# Revit family: Faucet_Touchless-Lavatory-KOHLER-Kumin-K-106K37
name_source: partatom
category: Plumbing Fixtures
units: mm (PartAtom-declared; Revit-internal decimal feet)

## family parameters
Cut with Voids When Loaded = No
Host = Face
OmniClass Number = 23.31.11.00
OmniClass Title = Faucets
Part Type = Normal
Room Calculation Point = No
Round Connector Dimension = Use Diameter
Shared = No

## types (5) — shared parameters
Assembly Code = D2010
CW Connection = Yes
Cold Water Inlet = Cold Water Inlet
Date Modified = 05/21/2024
Default Elevation = 36"
Description = Deck Mount Hybrid Mixing T
Drain Included = Yes
Electrical Note = Hybrid Energy Cell
HW Connection = Yes
Height = 5 1/16"
Hot Water Inlet = Hot Water Inlet
Length = 5 5/16"
Manufacturer = Kohler Co.
Master Format 2014 = 22 41 39
Master Format 2014 Name = Residential Faucets, Supplies, and Trim
Material = Premium Metal Construction
Pressure = 60.00 psi
Product Documentation Link = https://www.us.kohler.com
Product Name = Kumin
Product Page URL = http://www.us.kohler.com
Spout Reach = 5 5/16"
URL = https://www.us.kohler.com
Vent Connection = No
Waste Connection = No
Waste Water Outlet = Waste Water Outlet
WaterSense Certified = No
Width = 1 15/16"

## per-type parameters (varying)
| type | ADA Compliant | Finish | Flow Rate | Model | Type |
| 0.5 GPM, CP-Polished Chrome | Yes | Kohler-Metal-CP-Polished_Chrome | 1 GPM | K-106K37-SANA-CP | 4 |
| 0.5 GPM, BN-Vibrant Brushed Nickel | Yes | Kohler-Metal-BN-Vibrant_Brushed_Nickel | 1 GPM | K-106K37-SANA-BN | 3 |
| 0.5 GPM, BL-Matte Black | Yes | Kohler-Metal-BL-Matte_Black | 1 GPM | K-106K37-SANA-BL | 2 |
| 0.5 GPM, 2MB-Vibrant Brushed Moderne Brass | Yes | Kohler-Metal-2MB-Vibrant_Brushed_Moderne_Brass | 1 GPM | K-106K37-SANA-2MB | 1 |
| 0.35 GPM, CP-Polished Chrome | No | Kohler-Metal-CP-Polished_Chrome | 0 GPM | K-106K37-SATA-CP | 5 |

## geometry (parser evidence)
native form markers: Sweep x5
no freeform markers — native parametric forms only
